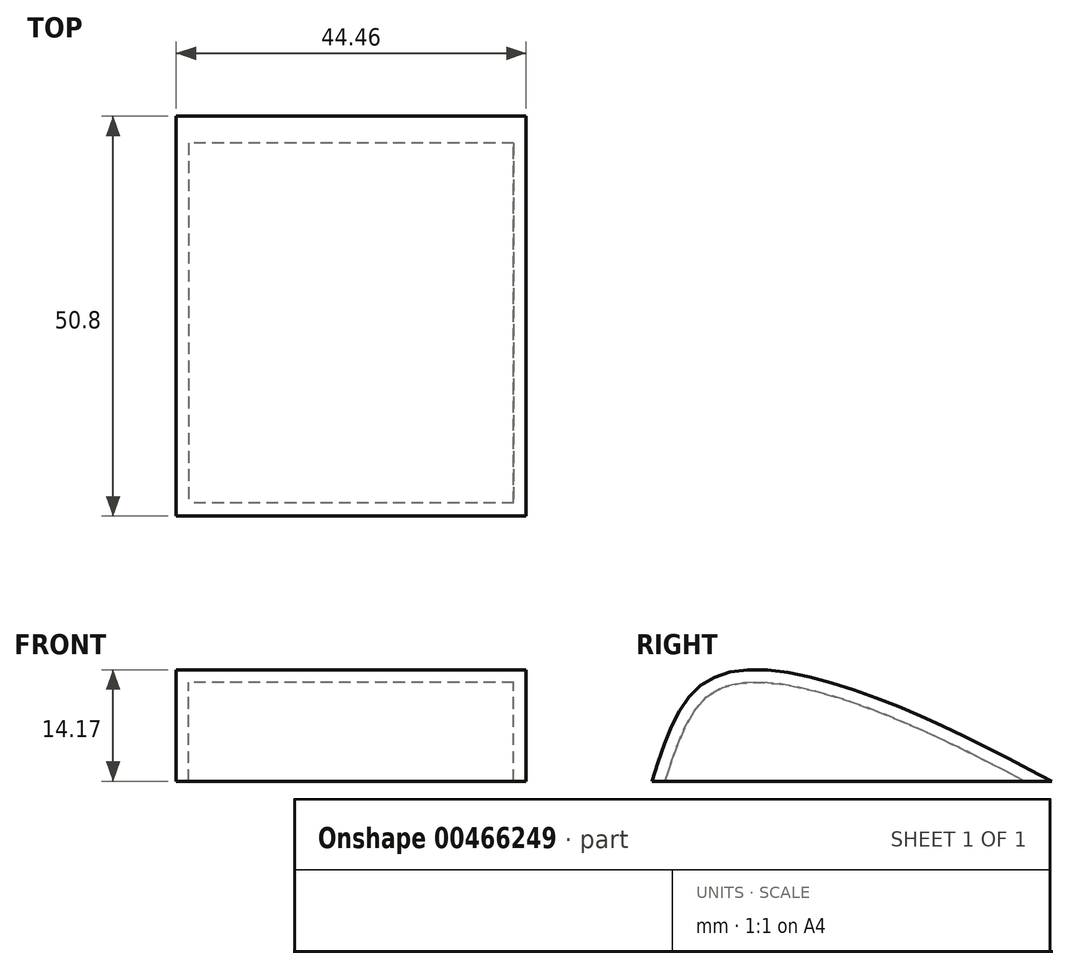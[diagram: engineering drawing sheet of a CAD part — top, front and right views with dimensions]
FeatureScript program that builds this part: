
annotation { "Feature Type Name" : "Feature", "Feature Type Description" : "" }
export const myFeature = defineFeature(function(context is Context, id is Id, definition is map)
    precondition{}
    {
        {
            var Q0;
            Q0=qCreatedBy(makeId("Top.planeOp"),FACE);
            var sketch = newSketch(context, id + "F0", { "sketchPlane" : qUnion([Q0])});
            skLineSegment(sketch, "E0.bottom", {"start": v(-22.23, 25.4) * mm, "end": v(22.23, 25.4) * mm});
            skLineSegment(sketch, "E0.top", {"start": v(-22.23, -25.4) * mm, "end": v(22.23, -25.4) * mm});
            skLineSegment(sketch, "E0.left", {"start": v(-22.23, 25.4) * mm, "end": v(-22.23, -25.4) * mm});
            skLineSegment(sketch, "E0.right", {"start": v(22.23, 25.4) * mm, "end": v(22.23, -25.4) * mm});
            skLineSegment(sketch, "E1", {"start": v(0, -25.4) * mm, "end": v(0, 25.4) * mm, "construction": true});
            skLineSegment(sketch, "E2", {"start": v(-22.23, 0) * mm, "end": v(22.23, 0) * mm, "construction": true});
            skSolve(sketch);
        }
        {
            var Q0;
            Q0 = qSketchRegion(id + "F0", true);
            extrude(context, id + "F1", {"entities" : qUnion([Q0]), "depth" : 19.05 * mm});
        }
        {
            var Q0;
            Q0=makeQuery(id+"F1.opExtrude","SWEPT_FACE",FACE,{"disambiguationData":[OSD([sQuery(id+"F0.wireOp",EDGE,"E0.left")])]});
            var sketch = newSketch(context, id + "F2", { "sketchPlane" : qUnion([Q0])});
            skFitSpline(sketch, "E3", {"points": [v(-25.4, 0) * mm, v(0, 11.7) * mm, v(18.3, 12.8) * mm, v(25.4, 0) * mm], "startDerivative": vector(63.92, 33.57) * mm, "endDerivative": vector(17.16, -55.48) * mm});
            skLineSegment(sketch, "E4", {"start": v(-25.4, 0) * mm, "end": v(-25.4, 19.05) * mm});
            skLineSegment(sketch, "E5", {"start": v(-25.4, 19.05) * mm, "end": v(25.4, 19.05) * mm});
            skSolve(sketch);
        }
        {
            var Q0;
            Q0=makeQuery(id+"F2.imprint","IMPRINT",FACE,{"disambiguationData":[TD([[makeQuery(id+"F2.imprint","IMPRINT",EDGE,{"derivedFrom":sQuery(id+"F2.wireOp",EDGE,"E3")}),1.0]])]});
            extrude(context, id + "F3", {"entities" : qUnion([Q0]), "operationType" : NewBodyOperationType.REMOVE, "endBound" : BoundingType.THROUGH_ALL, "oppositeDirection" : true, "depth" : 25.4 * mm});
        }
        {
            var Q0;
            Q0=makeQuery(id+"F1.opExtrude","CAP_FACE",FACE,{"disambiguationData":[OSD([sQuery(id+"F0.wireOp",EDGE,"E0.bottom"),sQuery(id+"F0.wireOp",EDGE,"E0.top"),sQuery(id+"F0.wireOp",EDGE,"E0.left"),sQuery(id+"F0.wireOp",EDGE,"E0.right")])],"isStart":true});
            shell(context, id + "F4", {"entities" : qUnion([Q0]), "thickness" : 1.59 * mm});
        }
    });
